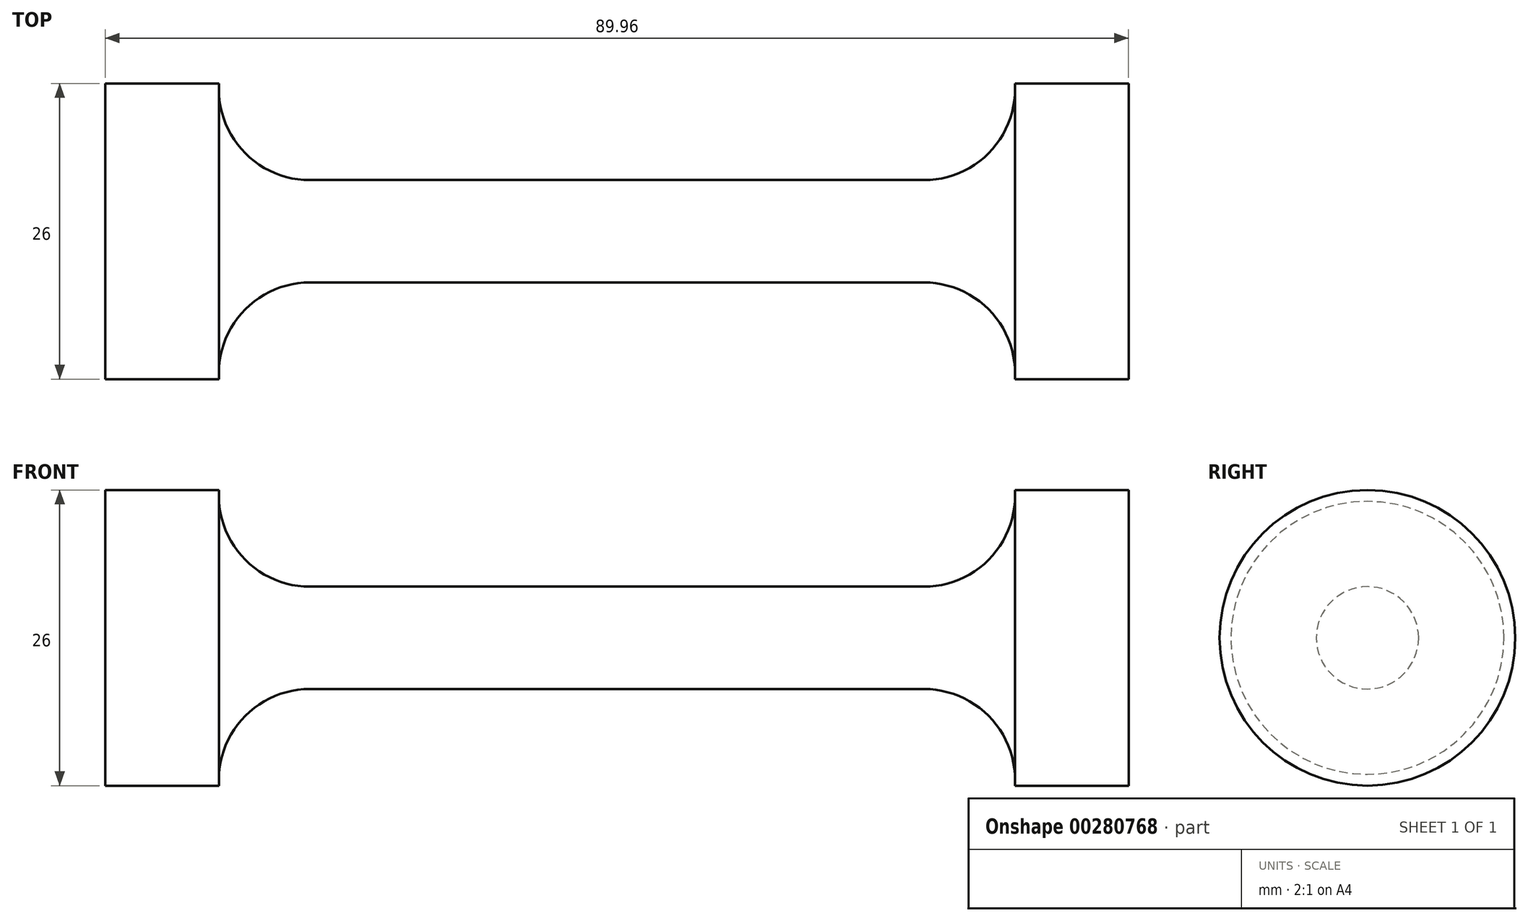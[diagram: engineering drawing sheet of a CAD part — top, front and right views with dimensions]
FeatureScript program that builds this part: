
annotation { "Feature Type Name" : "Feature", "Feature Type Description" : "" }
export const myFeature = defineFeature(function(context is Context, id is Id, definition is map)
    precondition{}
    {
        {
            var Q0;
            Q0=qCreatedBy(makeId("Front.planeOp"),FACE);
            var sketch = newSketch(context, id + "F0", { "sketchPlane" : qUnion([Q0])});
            skLineSegment(sketch, "E0", {"start": v(0, 4.5) * mm, "end": v(27, 4.5) * mm});
            skArc(sketch, "E1", {"start": v(27, 4.5) * mm, "mid": v(32.83, 7.02) * mm, "end": v(34.98, 13) * mm});
            skLineSegment(sketch, "E2", {"start": v(34.98, 13) * mm, "end": v(34.98, 0) * mm});
            skLineSegment(sketch, "E3.MirrorCS", {"start": v(34.98, -13) * mm, "end": v(34.98, 0) * mm});
            skArc(sketch, "E4.MirrorCS", {"start": v(27, -4.5) * mm, "mid": v(32.83, -7.02) * mm, "end": v(34.98, -13) * mm});
            skLineSegment(sketch, "E5.MirrorCS", {"start": v(0, 4.5) * mm, "end": v(-27, 4.5) * mm});
            skArc(sketch, "E6.MirrorCS", {"start": v(-27, 4.5) * mm, "mid": v(-32.83, 7.02) * mm, "end": v(-34.98, 13) * mm});
            skLineSegment(sketch, "E7.MirrorCS", {"start": v(-34.98, -13) * mm, "end": v(-34.98, 0) * mm});
            skArc(sketch, "E8.MirrorCS", {"start": v(-27, -4.5) * mm, "mid": v(-32.83, -7.02) * mm, "end": v(-34.98, -13) * mm});
            skLineSegment(sketch, "E9.MirrorCS", {"start": v(-34.98, 13) * mm, "end": v(-34.98, 0) * mm});
            skLineSegment(sketch, "E10", {"start": v(34.98, 13) * mm, "end": v(44.98, 13) * mm});
            skLineSegment(sketch, "E11", {"start": v(-34.98, 13) * mm, "end": v(-51.87, 13) * mm});
            skLineSegment(sketch, "E12", {"start": v(-44.98, -13) * mm, "end": v(-44.98, 13) * mm});
            skLineSegment(sketch, "E13", {"start": v(-44.98, 0) * mm, "end": v(44.98, 0) * mm});
            skLineSegment(sketch, "E14", {"start": v(44.98, 13) * mm, "end": v(44.98, 0) * mm});
            skSolve(sketch);
        }
        {
            var Q0;
            {var subQ0=sQuery(id+"F0.wireOp",EDGE,"E10");Q0=makeQuery(id+"F0.imprint","IMPRINT",FACE,{"disambiguationData":[TD([[makeQuery(id+"F0.imprint","IMPRINT",EDGE,{"derivedFrom":subQ0}),-1.0]])]});}
            var Q1;
            {var subQ1=sQuery(id+"F0.wireOp",EDGE,"E0");Q1=makeQuery(id+"F0.imprint","IMPRINT",FACE,{"disambiguationData":[TD([[makeQuery(id+"F0.imprint","IMPRINT",EDGE,{"derivedFrom":subQ1}),-1.0]])]});}
            var Q2;
            {var subQ3=sQuery(id+"F0.wireOp",EDGE,"E13");var subQ6=sQuery(id+"F0.wireOp",EDGE,"E9.MirrorCS");var subQ9=makeQuery(id+"F0.imprint","INTERSECT",VERTEX,{"derivedFrom":[subQ6,subQ3]});Q2=makeQuery(id+"F0.imprint","IMPRINT",FACE,{"disambiguationData":[TD([[makeQuery(id+"F0.imprint","IMPRINT",EDGE,{"disambiguationData":[TD([[subQ9,1.0]])],"derivedFrom":subQ6}),-1.0]])]});}
            var Q3;
            {var subQ0=sQuery(id+"F0.wireOp",EDGE,"E6.MirrorCS");var subQ1=sQuery(id+"F0.wireOp",EDGE,"E9.MirrorCS");var subQ3=makeQuery(id+"F0.imprint","INTERSECT",VERTEX,{"derivedFrom":[subQ1,subQ0]});Q3=makeQuery(id+"F0.imprint","IMPRINT",FACE,{"disambiguationData":[TD([[makeQuery(id+"F0.imprint","IMPRINT",EDGE,{"disambiguationData":[TD([[subQ3,1.0]])],"derivedFrom":subQ1}),-1.0]])]});}
            var Q4;
            {var subQ0=sQuery(id+"F0.wireOp",EDGE,"E2");var subQ1=sQuery(id+"F0.wireOp",EDGE,"E1");var subQ3=makeQuery(id+"F0.imprint","INTERSECT",VERTEX,{"derivedFrom":[subQ1,subQ0]});Q4=makeQuery(id+"F0.imprint","IMPRINT",FACE,{"disambiguationData":[TD([[makeQuery(id+"F0.imprint","IMPRINT",EDGE,{"disambiguationData":[TD([[subQ3,-1.0]])],"derivedFrom":subQ1}),1.0]])]});}
            var Q5;
            Q5=sQuery(id+"F0.wireOp",EDGE,"E13");
            revolve(context, id + "F1", {"entities" : qUnion([Q0, Q1, Q2, Q3, Q4]), "axis" : qUnion([Q5]), "revolveType" : RevolveType.FULL});
        }
    });
